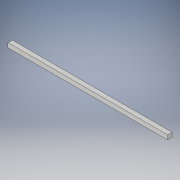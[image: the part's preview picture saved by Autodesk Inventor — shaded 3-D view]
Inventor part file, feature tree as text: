
AUTODESK INVENTOR PART (.ipt)
format: ipt  version: 2017 (Build 210142000, 142)  size: 92,672 bytes
history: native  units: in
note: dims shown in document units (in); Inventor stores cm internally (conversion verified against a paired STEP export)
features: extrude x1, sketch x1
ambient origin geometry x8: Origin, YZ Plane, XZ Plane, XY Plane, X Axis, Y Axis, Z Axis, Center Point
bodies: Solid1 (feature_tree)
feature tree (2):
  extrude  "Extrusion1"  Depth=0.25in
  sketch  "Sketch1"  dims[d0=9.0in d1=0.25in d2=0.25in d3=0.0in]
